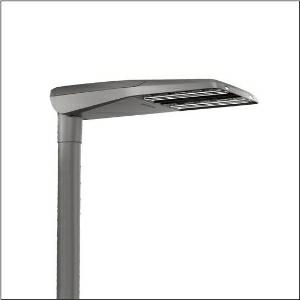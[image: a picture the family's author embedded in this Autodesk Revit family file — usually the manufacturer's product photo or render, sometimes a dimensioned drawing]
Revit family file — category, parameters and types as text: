
# Revit family: streetlight_sl_11_iq_midi___st1_0a_5xc3m41f08me_932e
name_source: partatom
category: Lighting Fixtures
units: mm (PartAtom-declared; Revit-internal decimal feet)

## family parameters
Cut with Voids When Loaded = No
Host = Face
Light Source = No
Part Type = Normal
Room Calculation Point = No
Round Connector Dimension = Use Diameter
Shared = No

## types (1)
- --- (1 x LED, 18310 lm, 124.7 W, 4000K)
    Apparent Load = 125 VA
    CIE Flux Codes = 33 66 96 100 100
    Color Rendering = 70
    Color Temperature = 4000K
    Default Elevation = 1800 mm
    Description = Streetlight SL 11 iQ midi, mast luminaire, primary light control with 3 zone facetted reflector, of plastic, silver coated, highly specular, primary optical cover: cover, of PMMA, transparent, light distribution: ST1.0a, light emission: direct distribution, primary light characteristic: asymmetric, installation type: post-top, side-entry, lamps: LED, High Power LED, rated values: 18.310lm | 124,7W | 146,8lm/W (begin service life); end service life: 18.310lm | 132,2W; at 50% lumin. flux: 9.155lm | 57,4W | 159,5lm/W, colour temperature: 4000K, colour rendering: CRI > 70, light colour: 740, light setting 1 begin service life: 100% | 18.310lm | 124,7W | 146,8lm/W | 4.000K, light setting 1 end service life: 132,2W, further light settings possible, control: optimised constant luminous flux control (CLO 2.0), Street-Remote, Desk-Remote (wireless, voltage-free reading and setting of iQ features in the workshop via application-optimized NFC function/RFID function), Light-Fading, Smart-Wire, Night-Set, Lumen-Switch, Temp-Guard, Auto-Match, with cable H07RN-F 3x 1.5mm², mains connection: 230..240V, AC, 50/60Hz, connection cable pre-assembled, cable length: 12,5m, luminaire housing, of diecast aluminium, powder-coated, SITECO metallic grey (DB 702S), please order mast flange separately, inclination adjustable without tools: 0°, 5°, 10°, 15° (post-top) | 0°, -5°, -10°, -15° (side-entry), sealing non-destructively replaceable, multi-level sealing system, length: 780mm, width: 376mm, height: 118mm, mast flange for spigot size: 42mm (side-entry): 5XC10008XM4, 60/48mm (side-entry/post-top): 5XC10108XM2, 76/60mm (side-entry/post-top): 5XC10108XM1, equipment: Power, protection rating (complete): IP66, insulation class (complete): insulation class II (safety insulation), certification: CE, ENEC, ENEC+, VDE, impact resistance: IK10, permissible operating ambient temperature for outdoor applications: -25..+50°C, standard-compliant lighting for roads and squares, Environmental Product Declaration (EPD) tested and certified by an independent institute, packaging unit: 1 piece

Light Distribution: ST1.0a
    Height = 118 mm
    Lamp = 1 x LED
    Lamp Light Flux = 18310 lm
    Lamp Power = 124.7 W
    Lamp count = 1
    Length = 780 mm
    Luminous efficacy = 147 lm/W
    Manufacturer = Siteco
    ModVariant = No
    Model = 5XC3M41F08ME
    Number of Poles = 1
    OnlyDefault = Yes
    Power Factor = 1
    Product Name = Streetlight SL 11 iQ midi | ST1.0a
    Product group = mast luminaire | pylon top
    ProductGroupID = 6100
    Protection Class = Protection class II
    Protection Degree = IP 66
    RLX_Detail_Level = 1
    RLX_Emergency_Light_Flux = 0 lm
    RLX_Emergency_Type = 0
    RLX_Emergency_Type_DB = No
    RlxData = <blob elided: 70421 chars, md5=886631a2>
    Socket = socket
    Standby Power = 0 W
    System Light Flux = 18310 lm
    System Power = 125 W
    Type Comments = factory setting: luminous flux: 100 % | dim-lin: 254 | 557 mA
    Type Image = l_1005960.jpg
    URL = http://relux.com
    VarID = @adj_092417
    Voltage = 0 V
    Weight = 0.00 kg
    Width = 376 mm

## geometry (parser evidence)
native form markers: Blend x4, Sweep x10
no freeform markers — native parametric forms only
